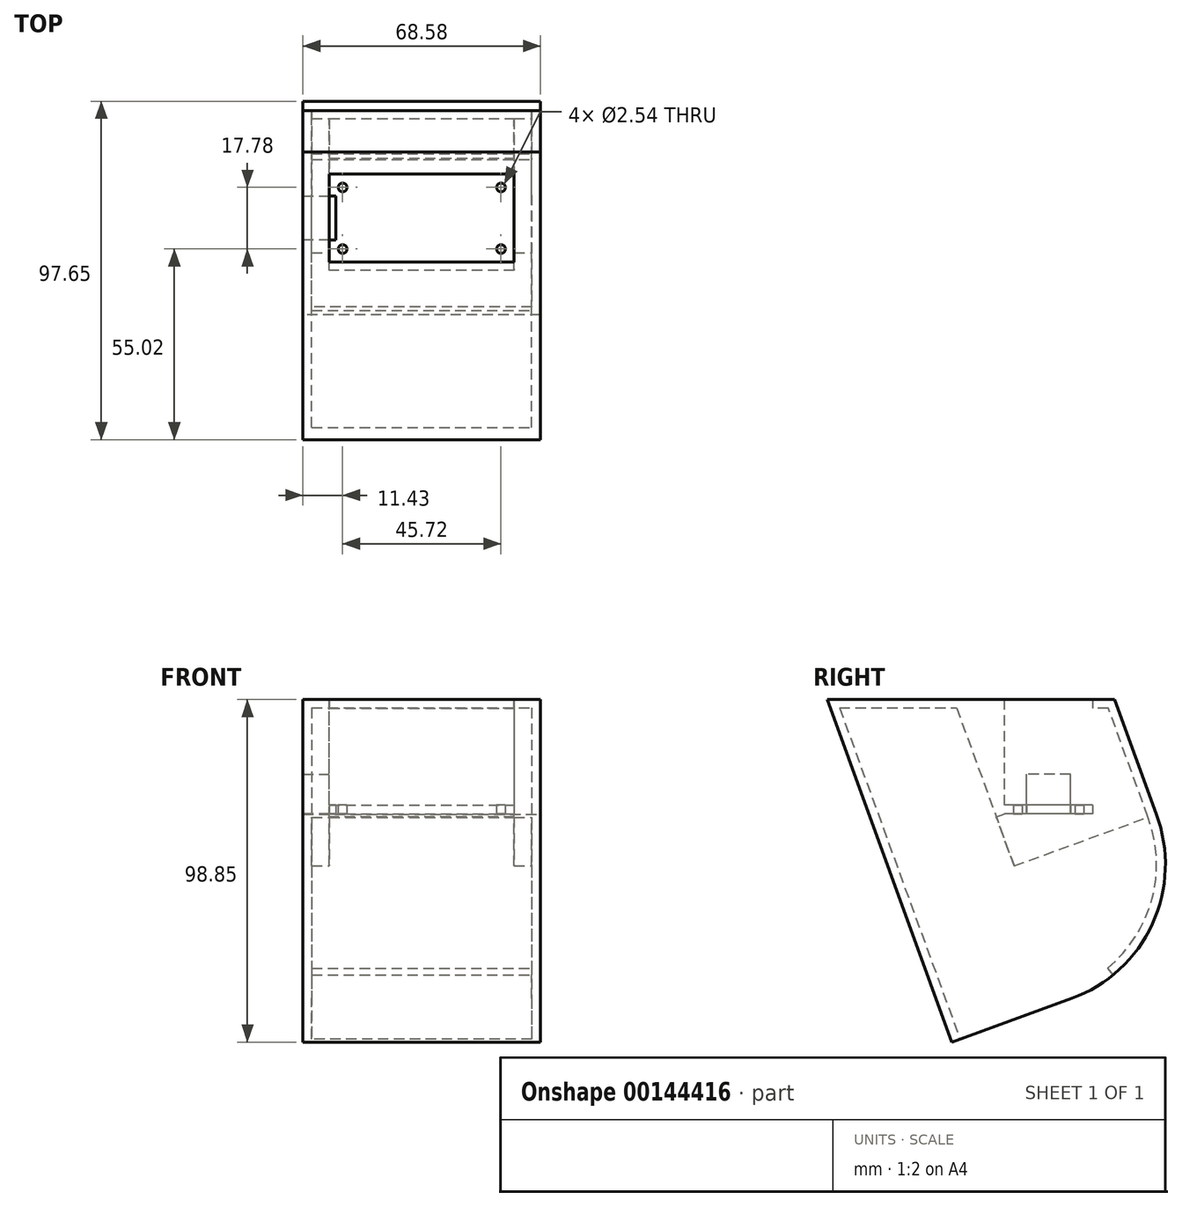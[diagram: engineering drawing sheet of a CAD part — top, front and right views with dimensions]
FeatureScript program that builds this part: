
annotation { "Feature Type Name" : "Feature", "Feature Type Description" : "" }
export const myFeature = defineFeature(function(context is Context, id is Id, definition is map)
    precondition{}
    {
        {
            var Q0;
            Q0=qCreatedBy(makeId("Top.planeOp"),FACE);
            var sketch = newSketch(context, id + "F0", { "sketchPlane" : qUnion([Q0])});
            skLineSegment(sketch, "E0.bottom", {"start": v(-26.67, 12.7) * mm, "end": v(26.67, 12.7) * mm});
            skLineSegment(sketch, "E0.top", {"start": v(-26.67, -12.7) * mm, "end": v(26.67, -12.7) * mm});
            skLineSegment(sketch, "E0.left", {"start": v(-26.67, 12.7) * mm, "end": v(-26.67, -12.7) * mm});
            skLineSegment(sketch, "E0.right", {"start": v(26.67, 12.7) * mm, "end": v(26.67, -12.7) * mm});
            skPoint(sketch, "E0.middle", {"position": v(0, 0) * mm});
            skLineSegment(sketch, "E1.bottom", {"start": v(-22.86, 8.89) * mm, "end": v(22.86, 8.89) * mm, "construction": true});
            skLineSegment(sketch, "E1.top", {"start": v(-22.86, -8.89) * mm, "end": v(22.86, -8.89) * mm, "construction": true});
            skLineSegment(sketch, "E1.left", {"start": v(-22.86, 8.89) * mm, "end": v(-22.86, -8.89) * mm, "construction": true});
            skLineSegment(sketch, "E1.right", {"start": v(22.86, 8.89) * mm, "end": v(22.86, -8.89) * mm, "construction": true});
            skCircle(sketch, "E2", {"center": v(-22.86, 8.89) * mm, "radius": 1.27 * mm});
            skCircle(sketch, "E3", {"center": v(22.86, 8.89) * mm, "radius": 1.27 * mm});
            skCircle(sketch, "E4", {"center": v(22.86, -8.89) * mm, "radius": 1.27 * mm});
            skCircle(sketch, "E5", {"center": v(-22.86, -8.89) * mm, "radius": 1.27 * mm});
            skSolve(sketch);
        }
        {
            var Q0;
            Q0=makeQuery(id+"F0.imprint","IMPRINT",FACE,{"disambiguationData":[TD([[makeQuery(id+"F0.imprint","IMPRINT",EDGE,{"derivedFrom":sQuery(id+"F0.wireOp",EDGE,"E0.bottom")}),-1.0]])]});
            extrude(context, id + "F1", {"entities" : qUnion([Q0]), "depth" : 2.54 * mm});
        }
        {
            var Q0;
            Q0=makeQuery(id+"F1.opExtrude","SWEPT_FACE",FACE,{"disambiguationData":[OSD([sQuery(id+"F0.wireOp",EDGE,"E0.right")])]});
            var sketch = newSketch(context, id + "F2", { "sketchPlane" : qUnion([Q0])});
            skLineSegment(sketch, "E6", {"start": v(-9.94, -15) * mm, "end": v(-15.24, -0.45) * mm});
            skLineSegment(sketch, "E7", {"start": v(-27.42, 33.02) * mm, "end": v(-12.7, 33.02) * mm});
            skLineSegment(sketch, "E8", {"start": v(-12.7, 33.02) * mm, "end": v(-12.7, 2.54) * mm});
            skLineSegment(sketch, "E9", {"start": v(12.7, 30.48) * mm, "end": v(12.7, 33.02) * mm});
            skLineSegment(sketch, "E10", {"start": v(12.7, 33.02) * mm, "end": v(19.05, 33.02) * mm});
            skLineSegment(sketch, "E11", {"start": v(12.7, 0) * mm, "end": v(-12.7, 0) * mm, "construction": true});
            skLineSegment(sketch, "E12", {"start": v(-12.7, 0) * mm, "end": v(-7.56, -14.13) * mm});
            skLineSegment(sketch, "E13", {"start": v(-7.56, -14.13) * mm, "end": v(-9.94, -15) * mm});
            skLineSegment(sketch, "E14", {"start": v(-12.7, 0) * mm, "end": v(-15.09, -0.87) * mm, "construction": true});
            skLineSegment(sketch, "E15", {"start": v(-26.5, 30.48) * mm, "end": v(-15.24, 30.48) * mm});
            skLineSegment(sketch, "E16", {"start": v(-15.24, 30.48) * mm, "end": v(-15.24, -0.45) * mm});
            skLineSegment(sketch, "E17", {"start": v(-15.24, 30.48) * mm, "end": v(-15.24, 33.02) * mm, "construction": true});
            skLineSegment(sketch, "E18", {"start": v(-15.24, 30.48) * mm, "end": v(-12.7, 30.48) * mm, "construction": true});
            skLineSegment(sketch, "E19.trimOffspring", {"start": v(-26.5, 30.48) * mm, "end": v(-27.42, 33.02) * mm});
            skLineSegment(sketch, "E20", {"start": v(19.05, 33.02) * mm, "end": v(31.1, -0.06) * mm});
            skLineSegment(sketch, "E21", {"start": v(12.7, 30.48) * mm, "end": v(17.27, 30.48) * mm});
            skLineSegment(sketch, "E22", {"start": v(17.27, 30.48) * mm, "end": v(17.27, 33.02) * mm, "construction": true});
            skLineSegment(sketch, "E23", {"start": v(12.7, 30.48) * mm, "end": v(12.7, 0) * mm, "construction": true});
            skLineSegment(sketch, "E24", {"start": v(17.27, 30.48) * mm, "end": v(28.7, -0.93) * mm});
            skLineSegment(sketch, "E25", {"start": v(31.1, -0.06) * mm, "end": v(28.7, -0.93) * mm});
            skLineSegment(sketch, "E26", {"start": v(-15.24, -0.45) * mm, "end": v(-26.5, 30.48) * mm});
            skSolve(sketch);
        }
        {
            var Q0;
            Q0=makeQuery(id+"F2.imprint","IMPRINT",FACE,{"disambiguationData":[TD([[makeQuery(id+"F2.imprint","IMPRINT",EDGE,{"derivedFrom":sQuery(id+"F2.wireOp",EDGE,"E6")}),-1.0]])]});
            var Q1;
            {var subQ0=sQuery(id+"F2.wireOp",EDGE,"E10");Q1=makeQuery(id+"F2.imprint","IMPRINT",FACE,{"disambiguationData":[TD([[makeQuery(id+"F2.imprint","IMPRINT",EDGE,{"derivedFrom":subQ0}),-1.0]])]});}
            var Q2;
            Q2=makeQuery(id+"F2.imprint","IMPRINT",FACE,{"disambiguationData":[TD([[makeQuery(id+"F2.imprint","IMPRINT",EDGE,{"derivedFrom":sQuery(id+"F2.wireOp",EDGE,"E15")}),-1.0]])]});
            var Q3;
            Q3=makeQuery(id+"F1.opExtrude","SWEPT_FACE",FACE,{"disambiguationData":[OSD([sQuery(id+"F0.wireOp",EDGE,"E0.left")])]});
            extrude(context, id + "F3", {"entities" : qUnion([Q0, Q1, Q2]), "operationType" : NewBodyOperationType.ADD, "endBound" : BoundingType.UP_TO_SURFACE, "oppositeDirection" : true, "endBoundEntityFace" : qUnion([Q3]), "depth" : 25.4 * mm});
        }
        {
            var Q0;
            {var subQ0=sQuery(id+"F0.wireOp",EDGE,"E0.right");Q0=makeQuery(id+"F3.boolean.opBoolean","MERGE",FACE,{"derivedFrom":[makeQuery(id+"F1.opExtrude","SWEPT_FACE",FACE,{"disambiguationData":[OSD([subQ0])]}),makeQuery(id+"F3.opExtrude","CAP_FACE",FACE,{"disambiguationData":[OSD([sQuery(id+"F0.wireOp",EDGE,"E0.top"),subQ0,sQuery(id+"F2.wireOp",EDGE,"E6"),sQuery(id+"F2.wireOp",EDGE,"E7"),sQuery(id+"F2.wireOp",EDGE,"E8"),sQuery(id+"F2.wireOp",EDGE,"E12"),sQuery(id+"F2.wireOp",EDGE,"E13"),sQuery(id+"F2.wireOp",EDGE,"E15"),sQuery(id+"F2.wireOp",EDGE,"E16"),sQuery(id+"F2.wireOp",EDGE,"E19.trimOffspring")])],"isStart":true}),makeQuery(id+"F3.opExtrude","CAP_FACE",FACE,{"disambiguationData":[OSD([sQuery(id+"F2.wireOp",EDGE,"E9"),sQuery(id+"F2.wireOp",EDGE,"E10"),sQuery(id+"F2.wireOp",EDGE,"SmmmvM9C-pUx6-SF9N-F7vJ-8UwaG4GGWs7p"),sQuery(id+"F2.wireOp",EDGE,"Lm9eWCCf-Ip9H-rHLX-Ktgn-ZaawhkfSE8xp"),sQuery(id+"F2.wireOp",EDGE,"sxds9xUV-2B4Y-A0uB-J39R-enatIO1BYxkk"),sQuery(id+"F2.wireOp",EDGE,"dQ5MnW9q-ANMN-4Y8t-rllq-uHYUm3hkEWIQ"),sQuery(id+"F2.wireOp",EDGE,"E11")])],"isStart":true})]});}
            var sketch = newSketch(context, id + "F4", { "sketchPlane" : qUnion([Q0])});
            skLineSegment(sketch, "E27", {"start": v(-9.94, -15) * mm, "end": v(-27.42, 33.02) * mm});
            skLineSegment(sketch, "E28", {"start": v(-27.42, 33.02) * mm, "end": v(19.05, 33.02) * mm});
            skLineSegment(sketch, "E29", {"start": v(19.05, 33.02) * mm, "end": v(19.05, 33.02) * mm});
            skLineSegment(sketch, "E30.0", {"start": v(19.05, 33.02) * mm, "end": v(31.1, -0.06) * mm});
            skLineSegment(sketch, "E31", {"start": v(31.1, -0.06) * mm, "end": v(-9.94, -15) * mm});
            skSolve(sketch);
        }
        {
            var Q0;
            Q0 = qSketchRegion(id + "F4", true);
            extrude(context, id + "F5", {"entities" : qUnion([Q0]), "operationType" : NewBodyOperationType.ADD, "depth" : 7.62 * mm});
        }
        {
            var Q0;
            {var subQ0=sQuery(id+"F0.wireOp",EDGE,"E0.left");Q0=makeQuery(id+"F3.boolean.opBoolean","MERGE",FACE,{"derivedFrom":[makeQuery(id+"F1.opExtrude","SWEPT_FACE",FACE,{"disambiguationData":[OSD([subQ0])]}),makeQuery(id+"F3.opExtrude","CAP_FACE",FACE,{"disambiguationData":[OSD([subQ0]),ownerDisambiguation([makeQuery(id+"F3.opExtrude","SWEPT_BODY",BODY,{"disambiguationData":[OSD([sQuery(id+"F0.wireOp",EDGE,"E0.top"),sQuery(id+"F0.wireOp",EDGE,"E0.right"),sQuery(id+"F2.wireOp",EDGE,"E6"),sQuery(id+"F2.wireOp",EDGE,"E7"),sQuery(id+"F2.wireOp",EDGE,"E8"),sQuery(id+"F2.wireOp",EDGE,"E12"),sQuery(id+"F2.wireOp",EDGE,"E13"),sQuery(id+"F2.wireOp",EDGE,"E15"),sQuery(id+"F2.wireOp",EDGE,"E16"),sQuery(id+"F2.wireOp",EDGE,"E19.trimOffspring")])]})])],"isStart":false}),makeQuery(id+"F3.opExtrude","CAP_FACE",FACE,{"disambiguationData":[OSD([subQ0]),ownerDisambiguation([makeQuery(id+"F3.opExtrude","SWEPT_BODY",BODY,{"disambiguationData":[OSD([sQuery(id+"F2.wireOp",EDGE,"E9"),sQuery(id+"F2.wireOp",EDGE,"E10"),sQuery(id+"F2.wireOp",EDGE,"SmmmvM9C-pUx6-SF9N-F7vJ-8UwaG4GGWs7p"),sQuery(id+"F2.wireOp",EDGE,"Lm9eWCCf-Ip9H-rHLX-Ktgn-ZaawhkfSE8xp"),sQuery(id+"F2.wireOp",EDGE,"sxds9xUV-2B4Y-A0uB-J39R-enatIO1BYxkk"),sQuery(id+"F2.wireOp",EDGE,"dQ5MnW9q-ANMN-4Y8t-rllq-uHYUm3hkEWIQ"),sQuery(id+"F2.wireOp",EDGE,"E11")])]})])],"isStart":false})]});}
            var sketch = newSketch(context, id + "F6", { "sketchPlane" : qUnion([Q0])});
            skLineSegment(sketch, "E32.bottom", {"start": v(-6.35, 2.54) * mm, "end": v(6.35, 2.54) * mm});
            skLineSegment(sketch, "E32.top", {"start": v(-6.35, 11.43) * mm, "end": v(6.35, 11.43) * mm});
            skLineSegment(sketch, "E32.left", {"start": v(-6.35, 2.54) * mm, "end": v(-6.35, 11.43) * mm});
            skLineSegment(sketch, "E32.right", {"start": v(6.35, 2.54) * mm, "end": v(6.35, 11.43) * mm});
            skLineSegment(sketch, "E33", {"start": v(0, 11.43) * mm, "end": v(0, 2.54) * mm, "construction": true});
            skLineSegment(sketch, "E34.0.0", {"start": v(27.42, 33.02) * mm, "end": v(9.94, -15) * mm});
            skLineSegment(sketch, "E34.0.1", {"start": v(9.94, -15) * mm, "end": v(-31.1, -0.06) * mm});
            skLineSegment(sketch, "E34.0.2", {"start": v(-31.1, -0.06) * mm, "end": v(-19.05, 33.02) * mm});
            skLineSegment(sketch, "E34.0.3", {"start": v(-19.05, 33.02) * mm, "end": v(27.42, 33.02) * mm});
            skSolve(sketch);
        }
        {
            var Q0;
            Q0 = qSketchRegion(id + "F6", true);
            extrude(context, id + "F7", {"entities" : qUnion([Q0]), "operationType" : NewBodyOperationType.ADD, "depth" : 7.62 * mm});
        }
        {
            var Q0;
            Q0=makeQuery(id+"F7.opExtrude","CAP_FACE",FACE,{"disambiguationData":[OSD([sQuery(id+"F6.wireOp",EDGE,"58987af6-52ed-49af-b887-d8bee7a76936.0.0"),sQuery(id+"F6.wireOp",EDGE,"58987af6-52ed-49af-b887-d8bee7a76936.0.1"),sQuery(id+"F6.wireOp",EDGE,"58987af6-52ed-49af-b887-d8bee7a76936.0.2"),sQuery(id+"F6.wireOp",EDGE,"58987af6-52ed-49af-b887-d8bee7a76936.0.3"),sQuery(id+"F6.wireOp",EDGE,"58987af6-52ed-49af-b887-d8bee7a76936.0.4"),sQuery(id+"F6.wireOp",EDGE,"E32.bottom"),sQuery(id+"F6.wireOp",EDGE,"E32.top"),sQuery(id+"F6.wireOp",EDGE,"E32.left"),sQuery(id+"F6.wireOp",EDGE,"E32.right")])],"isStart":false});
            var sketch = newSketch(context, id + "F8", { "sketchPlane" : qUnion([Q0])});
            skLineSegment(sketch, "E35.bottom", {"start": v(-6.35, 2.54) * mm, "end": v(6.35, 2.54) * mm});
            skLineSegment(sketch, "E35.top", {"start": v(-6.35, 0) * mm, "end": v(6.35, 0) * mm});
            skLineSegment(sketch, "E35.left", {"start": v(-6.35, 2.54) * mm, "end": v(-6.35, 0) * mm});
            skLineSegment(sketch, "E35.right", {"start": v(6.35, 2.54) * mm, "end": v(6.35, 0) * mm});
            skSolve(sketch);
        }
        {
            var Q0;
            Q0 = qSketchRegion(id + "F8", true);
            extrude(context, id + "F9", {"entities" : qUnion([Q0]), "operationType" : NewBodyOperationType.REMOVE, "oppositeDirection" : true, "depth" : 9.52 * mm});
        }
        {
            var Q0;
            Q0=makeQuery(id+"F7.boolean.opBoolean","MERGE",FACE,{"derivedFrom":[makeQuery(id+"F5.boolean.opBoolean","MERGE",FACE,{"derivedFrom":[makeQuery(id+"F3.opExtrude","SWEPT_FACE",FACE,{"disambiguationData":[OSD([sQuery(id+"F2.wireOp",EDGE,"E6"),sQuery(id+"F2.wireOp",EDGE,"E19.trimOffspring"),sQuery(id+"F2.wireOp",EDGE,"E26")])]}),makeQuery(id+"F5.opExtrude","SWEPT_FACE",FACE,{"disambiguationData":[OSD([sQuery(id+"F4.wireOp",EDGE,"E27")])]})]}),makeQuery(id+"F7.opExtrude","SWEPT_FACE",FACE,{"disambiguationData":[OSD([sQuery(id+"F6.wireOp",EDGE,"E34.0.0")])]})]});
            var sketch = newSketch(context, id + "F10", { "sketchPlane" : qUnion([Q0])});
            skLineSegment(sketch, "E36.bottom", {"start": v(34.29, -10.7) * mm, "end": v(-34.3, -10.7) * mm});
            skLineSegment(sketch, "E36.top", {"start": v(34.3, -52.3) * mm, "end": v(-34.3, -52.3) * mm});
            skLineSegment(sketch, "E36.left", {"start": v(34.3, -10.7) * mm, "end": v(34.3, -52.3) * mm});
            skLineSegment(sketch, "E36.right", {"start": v(-34.3, -10.7) * mm, "end": v(-34.3, -52.3) * mm});
            skSolve(sketch);
        }
        {
            var Q0;
            Q0=makeQuery(id+"F10.imprint","IMPRINT",FACE,{"disambiguationData":[TD([[makeQuery(id+"F10.imprint","IMPRINT",EDGE,{"derivedFrom":sQuery(id+"F10.wireOp",EDGE,"E36.bottom")}),-1.0]])]});
            var Q1;
            Q1=makeQuery(id+"F3.opExtrude","SWEPT_FACE",FACE,{"disambiguationData":[OSD([sQuery(id+"F2.wireOp",EDGE,"E12")])]});
            extrude(context, id + "F11", {"entities" : qUnion([Q0]), "operationType" : NewBodyOperationType.ADD, "endBound" : BoundingType.UP_TO_SURFACE, "oppositeDirection" : true, "endBoundEntityFace" : qUnion([Q1]), "depth" : 25.4 * mm});
        }
        {
            var Q0;
            Q0=makeQuery(id+"F11.opExtrude","SWEPT_FACE",FACE,{"disambiguationData":[OSD([sQuery(id+"F10.wireOp",EDGE,"E36.top")])]});
            var sketch = newSketch(context, id + "F12", { "sketchPlane" : qUnion([Q0])});
            skLineSegment(sketch, "E37", {"start": v(34.3, 14.47) * mm, "end": v(34.3, 48.76) * mm});
            skLineSegment(sketch, "E38", {"start": v(34.3, 48.76) * mm, "end": v(-34.3, 48.76) * mm});
            skLineSegment(sketch, "E39", {"start": v(-34.3, 48.76) * mm, "end": v(-34.3, 14.47) * mm});
            skLineSegment(sketch, "E40.0", {"start": v(-31.75, 46.22) * mm, "end": v(-31.75, 14.47) * mm});
            skLineSegment(sketch, "E40.1", {"start": v(31.75, 46.22) * mm, "end": v(-31.75, 46.22) * mm});
            skLineSegment(sketch, "E40.2", {"start": v(31.75, 14.47) * mm, "end": v(31.75, 46.22) * mm});
            skLineSegment(sketch, "E41", {"start": v(31.75, 14.47) * mm, "end": v(34.3, 14.47) * mm});
            skLineSegment(sketch, "E42", {"start": v(-31.75, 14.47) * mm, "end": v(-34.3, 14.47) * mm});
            skSolve(sketch);
        }
        {
            var Q0;
            Q0 = qSketchRegion(id + "F12", true);
            var Q1;
            Q1=makeQuery(id+"F7.boolean.opBoolean","MERGE",FACE,{"derivedFrom":[makeQuery(id+"F5.boolean.opBoolean","MERGE",FACE,{"derivedFrom":[makeQuery(id+"F3.opExtrude","SWEPT_FACE",FACE,{"disambiguationData":[OSD([sQuery(id+"F2.wireOp",EDGE,"E7")])]}),makeQuery(id+"F3.opExtrude","SWEPT_FACE",FACE,{"disambiguationData":[OSD([sQuery(id+"F2.wireOp",EDGE,"E10")])]}),makeQuery(id+"F5.opExtrude","SWEPT_FACE",FACE,{"disambiguationData":[OSD([sQuery(id+"F4.wireOp",EDGE,"E28")])]})]}),makeQuery(id+"F7.opExtrude","SWEPT_FACE",FACE,{"disambiguationData":[OSD([sQuery(id+"F6.wireOp",EDGE,"E34.0.3")])]})]});
            extrude(context, id + "F13", {"entities" : qUnion([Q0]), "operationType" : NewBodyOperationType.ADD, "endBound" : BoundingType.UP_TO_SURFACE, "oppositeDirection" : true, "endBoundEntityFace" : qUnion([Q1]), "depth" : 25.4 * mm});
        }
        {
            var Q0;
            Q0=makeQuery(id+"F13.opExtrude","SWEPT_FACE",FACE,{"disambiguationData":[OSD([sQuery(id+"F12.wireOp",EDGE,"E40.2")])]});
            var sketch = newSketch(context, id + "F14", { "sketchPlane" : qUnion([Q0])});
            skLineSegment(sketch, "E43", {"start": v(26.55, 30.63) * mm, "end": v(27.42, 33.02) * mm});
            skLineSegment(sketch, "E44", {"start": v(27.42, 33.02) * mm, "end": v(61.2, 33.02) * mm});
            skLineSegment(sketch, "E45", {"start": v(61.2, 33.02) * mm, "end": v(60.34, 30.63) * mm});
            skLineSegment(sketch, "E46", {"start": v(60.34, 30.63) * mm, "end": v(26.55, 30.63) * mm});
            skSolve(sketch);
        }
        {
            var Q0;
            Q0 = qSketchRegion(id + "F14", true);
            extrude(context, id + "F15", {"entities" : qUnion([Q0]), "operationType" : NewBodyOperationType.ADD, "endBound" : BoundingType.UP_TO_NEXT, "depth" : 25.4 * mm});
        }
        {
            var Q0;
            {var subQ0=sQuery(id+"F2.wireOp",EDGE,"E12");Q0=makeQuery(id+"F11.boolean.opBoolean","MERGE",FACE,{"derivedFrom":[makeQuery(id+"F3.opExtrude","SWEPT_FACE",FACE,{"disambiguationData":[OSD([subQ0])]}),makeQuery(id+"F11.opExtrude","CAP_FACE",FACE,{"disambiguationData":[OSD([subQ0])],"isStart":false})]});}
            var sketch = newSketch(context, id + "F16", { "sketchPlane" : qUnion([Q0])});
            skLineSegment(sketch, "E47", {"start": v(-26.67, 4.34) * mm, "end": v(-26.67, -10.7) * mm});
            skLineSegment(sketch, "E48", {"start": v(-26.67, -10.7) * mm, "end": v(-31.75, -10.7) * mm});
            skLineSegment(sketch, "E49", {"start": v(-31.75, -10.7) * mm, "end": v(-31.75, -52.3) * mm});
            skLineSegment(sketch, "E50", {"start": v(-31.75, -52.3) * mm, "end": v(31.75, -52.3) * mm});
            skLineSegment(sketch, "E51", {"start": v(31.75, -52.3) * mm, "end": v(31.75, -10.7) * mm});
            skLineSegment(sketch, "E52", {"start": v(31.75, -10.7) * mm, "end": v(26.67, -10.7) * mm});
            skLineSegment(sketch, "E53", {"start": v(26.67, -10.7) * mm, "end": v(26.67, 4.34) * mm});
            skLineSegment(sketch, "E54", {"start": v(26.67, 4.34) * mm, "end": v(-26.67, 4.34) * mm});
            skSolve(sketch);
        }
        {
            var Q0;
            Q0 = qSketchRegion(id + "F16", true);
            extrude(context, id + "F17", {"entities" : qUnion([Q0]), "operationType" : NewBodyOperationType.REMOVE, "endBound" : BoundingType.UP_TO_NEXT, "oppositeDirection" : true, "depth" : 25.4 * mm});
        }
        {
            var Q0;
            Q0=makeQuery(id+"F13.boolean.opBoolean","MERGE",FACE,{"derivedFrom":[makeQuery(id+"F11.boolean.opBoolean","MERGE",FACE,{"derivedFrom":[makeQuery(id+"F5.opExtrude","CAP_FACE",FACE,{"disambiguationData":[OSD([sQuery(id+"F4.wireOp",EDGE,"E27"),sQuery(id+"F4.wireOp",EDGE,"E28"),sQuery(id+"F4.wireOp",EDGE,"E30.0"),sQuery(id+"F4.wireOp",EDGE,"E31")])],"isStart":false}),makeQuery(id+"F11.opExtrude","SWEPT_FACE",FACE,{"disambiguationData":[OSD([sQuery(id+"F10.wireOp",EDGE,"E36.left")])]})]}),makeQuery(id+"F13.opExtrude","SWEPT_FACE",FACE,{"disambiguationData":[OSD([sQuery(id+"F12.wireOp",EDGE,"E37")])]})]});
            var sketch = newSketch(context, id + "F18", { "sketchPlane" : qUnion([Q0])});
            skLineSegment(sketch, "E55", {"start": v(31.1, -0.06) * mm, "end": v(-7.56, -14.13) * mm});
            skLineSegment(sketch, "E56", {"start": v(-7.56, -14.13) * mm, "end": v(6.67, -53.23) * mm});
            skArc(sketch, "E57", {"start": v(6.67, -53.23) * mm, "mid": v(29.98, -31.75) * mm, "end": v(31.1, -0.06) * mm});
            skSolve(sketch);
        }
        {
            var Q0;
            Q0 = qSketchRegion(id + "F18", true);
            extrude(context, id + "F19", {"entities" : qUnion([Q0]), "operationType" : NewBodyOperationType.ADD, "oppositeDirection" : true, "depth" : 2.54 * mm});
        }
        {
            var Q0;
            Q0=makeQuery(id+"F13.boolean.opBoolean","MERGE",FACE,{"derivedFrom":[makeQuery(id+"F11.boolean.opBoolean","MERGE",FACE,{"derivedFrom":[makeQuery(id+"F7.opExtrude","CAP_FACE",FACE,{"disambiguationData":[OSD([sQuery(id+"F6.wireOp",EDGE,"E32.bottom"),sQuery(id+"F6.wireOp",EDGE,"E32.top"),sQuery(id+"F6.wireOp",EDGE,"E32.left"),sQuery(id+"F6.wireOp",EDGE,"E32.right"),sQuery(id+"F6.wireOp",EDGE,"E34.0.0"),sQuery(id+"F6.wireOp",EDGE,"E34.0.1"),sQuery(id+"F6.wireOp",EDGE,"E34.0.2"),sQuery(id+"F6.wireOp",EDGE,"E34.0.3")])],"isStart":false}),makeQuery(id+"F11.opExtrude","SWEPT_FACE",FACE,{"disambiguationData":[OSD([sQuery(id+"F10.wireOp",EDGE,"E36.right")])]})]}),makeQuery(id+"F13.opExtrude","SWEPT_FACE",FACE,{"disambiguationData":[OSD([sQuery(id+"F12.wireOp",EDGE,"E39")])]})]});
            var sketch = newSketch(context, id + "F20", { "sketchPlane" : qUnion([Q0])});
            skArc(sketch, "E58.0", {"start": v(-6.67, -53.23) * mm, "mid": v(-29.98, -31.75) * mm, "end": v(-31.1, -0.06) * mm});
            skLineSegment(sketch, "E59.0", {"start": v(7.56, -14.13) * mm, "end": v(-31.1, -0.06) * mm});
            skLineSegment(sketch, "E60.0", {"start": v(-6.67, -53.23) * mm, "end": v(7.56, -14.13) * mm});
            skSolve(sketch);
        }
        {
            var Q0;
            Q0 = qSketchRegion(id + "F20", true);
            extrude(context, id + "F21", {"entities" : qUnion([Q0]), "operationType" : NewBodyOperationType.ADD, "oppositeDirection" : true, "depth" : 2.54 * mm});
        }
        {
            var Q0;
            Q0=makeQuery(id+"F17.boolean.opBoolean","MERGE",FACE,{"derivedFrom":[makeQuery(id+"F7.boolean.opBoolean","MERGE",FACE,{"derivedFrom":[makeQuery(id+"F5.boolean.opBoolean","MERGE",FACE,{"derivedFrom":[makeQuery(id+"F3.opExtrude","SWEPT_FACE",FACE,{"disambiguationData":[OSD([sQuery(id+"F2.wireOp",EDGE,"E13")])]}),makeQuery(id+"F3.opExtrude","SWEPT_FACE",FACE,{"disambiguationData":[OSD([sQuery(id+"F2.wireOp",EDGE,"E25")])]}),makeQuery(id+"F5.opExtrude","SWEPT_FACE",FACE,{"disambiguationData":[OSD([sQuery(id+"F4.wireOp",EDGE,"E31")])]})]}),makeQuery(id+"F7.opExtrude","SWEPT_FACE",FACE,{"disambiguationData":[OSD([sQuery(id+"F6.wireOp",EDGE,"E34.0.1")])]})]}),makeQuery(id+"F17.opExtrude","SWEPT_FACE",FACE,{"disambiguationData":[OSD([sQuery(id+"F16.wireOp",EDGE,"E48")])]}),makeQuery(id+"F17.opExtrude","SWEPT_FACE",FACE,{"disambiguationData":[OSD([sQuery(id+"F16.wireOp",EDGE,"E52")])]})]});
            var sketch = newSketch(context, id + "F22", { "sketchPlane" : qUnion([Q0])});
            skLineSegment(sketch, "E61.bottom", {"start": v(31.75, -26.65) * mm, "end": v(-31.75, -26.65) * mm});
            skLineSegment(sketch, "E61.top", {"start": v(31.75, -29.2) * mm, "end": v(-31.75, -29.2) * mm});
            skLineSegment(sketch, "E61.left", {"start": v(31.75, -26.65) * mm, "end": v(31.75, -29.2) * mm});
            skLineSegment(sketch, "E61.right", {"start": v(-31.75, -26.65) * mm, "end": v(-31.75, -29.2) * mm});
            skSolve(sketch);
        }
        {
            var Q0;
            Q0=makeQuery(id+"F19.boolean.opBoolean","MERGE",FACE,{"derivedFrom":[makeQuery(id+"F17.boolean.opBoolean","MERGE",FACE,{"derivedFrom":[makeQuery(id+"F13.opExtrude","SWEPT_FACE",FACE,{"disambiguationData":[OSD([sQuery(id+"F12.wireOp",EDGE,"E40.2")])]}),makeQuery(id+"F17.opExtrude","SWEPT_FACE",FACE,{"disambiguationData":[OSD([sQuery(id+"F16.wireOp",EDGE,"E49")])]})]}),makeQuery(id+"F19.opExtrude","CAP_FACE",FACE,{"disambiguationData":[OSD([sQuery(id+"F18.wireOp",EDGE,"E55"),sQuery(id+"F18.wireOp",EDGE,"E56"),sQuery(id+"F18.wireOp",EDGE,"E57")])],"isStart":false})]});
            var sketch = newSketch(context, id + "F23", { "sketchPlane" : qUnion([Q0])});
            skArc(sketch, "E62.0", {"start": v(-18.58, -46.47) * mm, "mid": v(-32.32, -25.28) * mm, "end": v(-31.1, -0.06) * mm});
            skPoint(sketch, "E63", {"position": v(-18.58, -46.47) * mm});
            skPoint(sketch, "E64.orphan", {"position": v(-6.67, -53.23) * mm});
            skSolve(sketch);
        }
        {
            var Q0;
            Q0 = qSketchRegion(id + "F22", true);
            var Q1;
            Q1=sQuery(id+"F23.wireOp",EDGE,"E62.0");
            sweep(context, id + "F24", {"operationType" : NewBodyOperationType.ADD, "profiles" : qUnion([Q0]), "path" : qUnion([Q1])});
        }
    });
